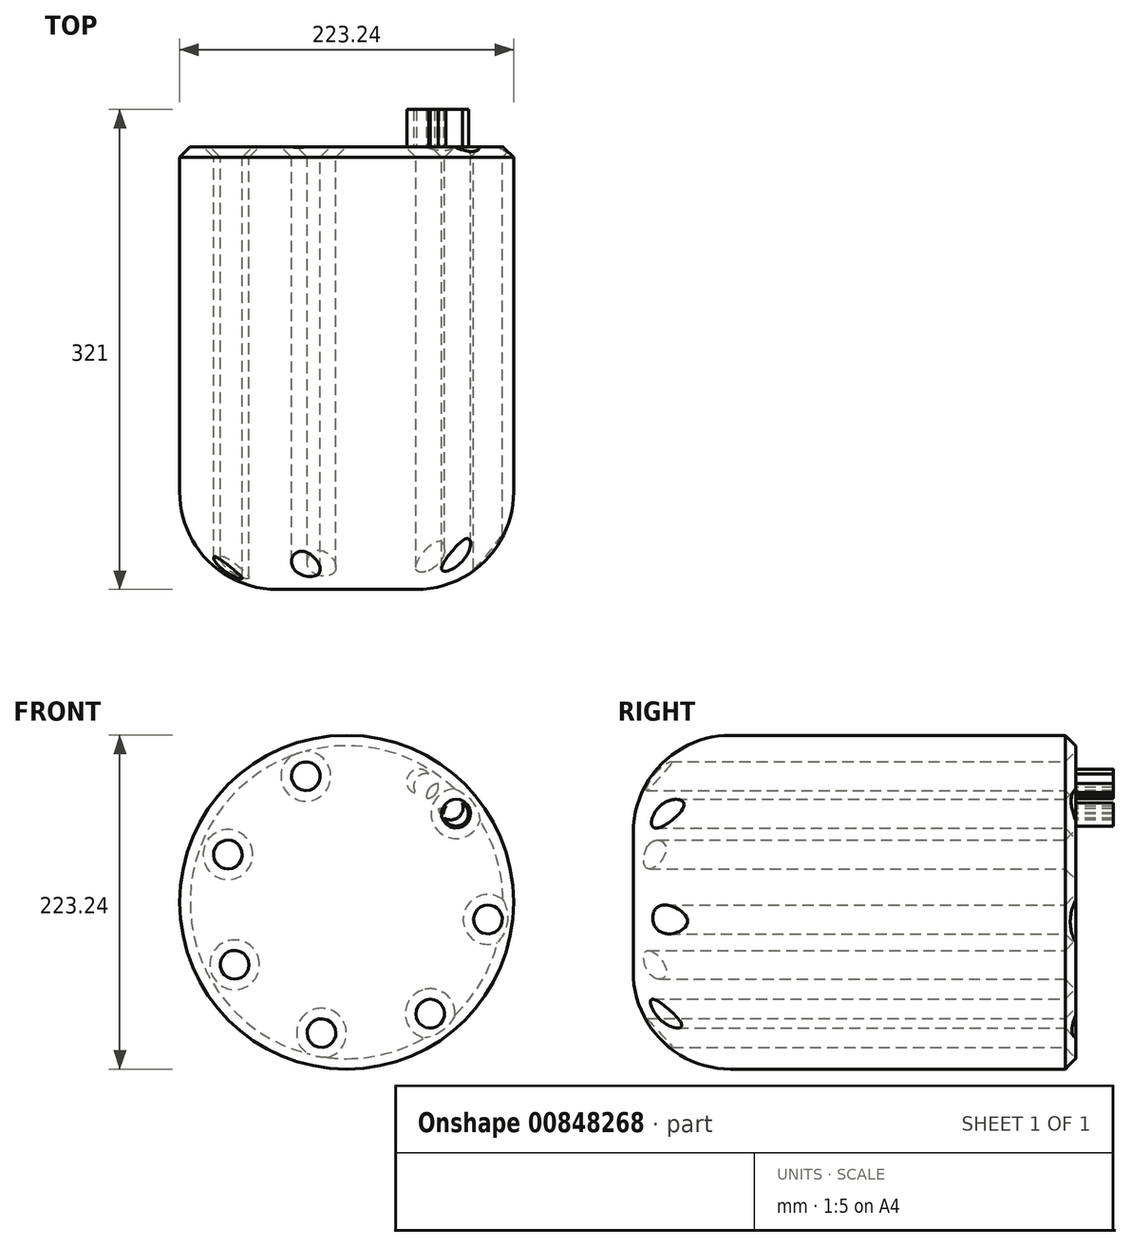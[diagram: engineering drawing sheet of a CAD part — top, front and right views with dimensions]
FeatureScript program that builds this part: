
annotation { "Feature Type Name" : "Feature", "Feature Type Description" : "" }
export const myFeature = defineFeature(function(context is Context, id is Id, definition is map)
    precondition{}
    {
        {
            var Q0;
            Q0=qCreatedBy(makeId("Front.planeOp"),FACE);
            var sketch = newSketch(context, id + "F0", { "sketchPlane" : qUnion([Q0])});
            skCircle(sketch, "E0", {"center": v(0, 0) * mm, "radius": 111.62 * mm});
            skCircle(sketch, "E1", {"center": v(73.16, 59.18) * mm, "radius": 9.64 * mm});
            skCircle(sketch, "E2.1.0", {"center": v(94.52, -11.55) * mm, "radius": 9.64 * mm});
            skCircle(sketch, "E2.2.0", {"center": v(55.9, -74.53) * mm, "radius": 9.64 * mm});
            skPoint(sketch, "E2.center", {"position": v(5.03, 0) * mm});
            skLineSegment(sketch, "E2.anchor1", {"start": v(5.03, 0) * mm, "end": v(73.16, 59.18) * mm, "construction": true});
            skLineSegment(sketch, "E2.anchor2", {"start": v(5.03, 0) * mm, "end": v(-27.28, 84.26) * mm, "construction": true});
            skCircle(sketch, "E3.1.3.0", {"center": v(-16.83, -87.55) * mm, "radius": 9.64 * mm});
            skCircle(sketch, "E3.1.4.0", {"center": v(-74.9, -41.87) * mm, "radius": 9.64 * mm});
            skCircle(sketch, "E4.1.5.0", {"center": v(-79.39, 31.88) * mm, "radius": 9.64 * mm});
            skCircle(sketch, "E4.1.6.0", {"center": v(-27.28, 84.26) * mm, "radius": 9.64 * mm});
            skSolve(sketch);
        }
        {
            var Q0;
            Q0=makeQuery(id+"F0.imprint","IMPRINT",FACE,{"disambiguationData":[TD([[makeQuery(id+"F0.imprint","IMPRINT",EDGE,{"derivedFrom":sQuery(id+"F0.wireOp",EDGE,"E0")}),1.0]])]});
            extrude(context, id + "F1", {"entities" : qUnion([Q0]), "depth" : 296 * mm, "offsetDistance" : 25 * mm});
        }
        {
            var Q0;
            Q0=makeQuery(id+"F1.opExtrude","CAP_EDGE",EDGE,{"disambiguationData":[OSD([sQuery(id+"F0.wireOp",EDGE,"E0")])],"isStart":false});
            fillet(context, id + "F2", {"entities" : qUnion([Q0]), "radius" : 65.18 * mm, "tangentPropagation" : true, "allowEdgeOverflow" : false});
        }
        {
            var Q0;
            Q0=makeQuery(id+"F1.opExtrude","CAP_EDGE",EDGE,{"disambiguationData":[OSD([sQuery(id+"F0.wireOp",EDGE,"E4.1.6.0")])],"isStart":true});
            var Q1;
            Q1=makeQuery(id+"F1.opExtrude","CAP_EDGE",EDGE,{"disambiguationData":[OSD([sQuery(id+"F0.wireOp",EDGE,"E4.1.5.0")])],"isStart":true});
            var Q2;
            Q2=makeQuery(id+"F1.opExtrude","CAP_FACE",FACE,{"disambiguationData":[OSD([sQuery(id+"F0.wireOp",EDGE,"E0"),sQuery(id+"F0.wireOp",EDGE,"E1"),sQuery(id+"F0.wireOp",EDGE,"E2.1.0"),sQuery(id+"F0.wireOp",EDGE,"E2.2.0"),sQuery(id+"F0.wireOp",EDGE,"E3.1.3.0"),sQuery(id+"F0.wireOp",EDGE,"E3.1.4.0"),sQuery(id+"F0.wireOp",EDGE,"E4.1.5.0"),sQuery(id+"F0.wireOp",EDGE,"E4.1.6.0")])],"isStart":true});
            chamfer(context, id + "F3", {"entities" : qUnion([Q0, Q1, Q2]), "width" : 7 * mm, "tangentPropagation" : true});
        }
        {
            var Q0;
            Q0=makeQuery(id+"F1.opExtrude","CAP_FACE",FACE,{"disambiguationData":[OSD([sQuery(id+"F0.wireOp",EDGE,"E0"),sQuery(id+"F0.wireOp",EDGE,"E1"),sQuery(id+"F0.wireOp",EDGE,"E2.1.0"),sQuery(id+"F0.wireOp",EDGE,"E2.2.0"),sQuery(id+"F0.wireOp",EDGE,"E3.1.3.0"),sQuery(id+"F0.wireOp",EDGE,"E3.1.4.0"),sQuery(id+"F0.wireOp",EDGE,"E4.1.5.0"),sQuery(id+"F0.wireOp",EDGE,"E4.1.6.0")])],"isStart":true});
            var sketch = newSketch(context, id + "F4", { "sketchPlane" : qUnion([Q0])});
            skCircle(sketch, "E5", {"center": v(-73.16, 59.18) * mm, "radius": 8.3 * mm});
            skCircle(sketch, "E6.1.0", {"center": v(-69.6, 63.33) * mm, "radius": 8.3 * mm});
            skCircle(sketch, "E6.2.0", {"center": v(-65.8, 67.27) * mm, "radius": 8.3 * mm});
            skCircle(sketch, "E6.3.0", {"center": v(-61.77, 70.98) * mm, "radius": 8.3 * mm});
            skCircle(sketch, "E6.4.0", {"center": v(-57.54, 74.45) * mm, "radius": 8.3 * mm});
            skCircle(sketch, "E6.5.0", {"center": v(-53.11, 77.67) * mm, "radius": 8.3 * mm});
            skCircle(sketch, "E6.6.0", {"center": v(-48.5, 80.63) * mm, "radius": 8.3 * mm});
            skPoint(sketch, "E6.center", {"position": v(0, 0) * mm});
            skLineSegment(sketch, "E6.anchor1", {"start": v(0, 0) * mm, "end": v(-73.16, 59.18) * mm, "construction": true});
            skLineSegment(sketch, "E6.anchor2", {"start": v(0, 0) * mm, "end": v(-48.5, 80.63) * mm, "construction": true});
            skSolve(sketch);
        }
        {
            var Q0;
            {var subQ0=sQuery(id+"F4.wireOp",EDGE,"E6.6.0");var subQ1=sQuery(id+"F4.wireOp",EDGE,"E6.5.0");var subQ2=makeQuery(id+"F4.imprint","INTERSECT",VERTEX,{"disambiguationData":[OD(0.0)],"derivedFrom":[subQ1,subQ0]});Q0=makeQuery(id+"F4.imprint","IMPRINT",FACE,{"disambiguationData":[TD([[makeQuery(id+"F4.imprint","IMPRINT",EDGE,{"disambiguationData":[TD([[subQ2,1.0]])],"derivedFrom":subQ1}),-1.0]])]});}
            var Q1;
            {var subQ3=sQuery(id+"F4.wireOp",EDGE,"E6.5.0");var subQ7=sQuery(id+"F4.wireOp",EDGE,"E6.2.0");var subQ9=makeQuery(id+"F4.imprint","INTERSECT",VERTEX,{"disambiguationData":[OD(0.0)],"derivedFrom":[subQ7,subQ3]});Q1=makeQuery(id+"F4.imprint","IMPRINT",FACE,{"disambiguationData":[TD([[makeQuery(id+"F4.imprint","IMPRINT",EDGE,{"disambiguationData":[TD([[subQ9,-1.0]])],"derivedFrom":subQ7}),-1.0]])]});}
            var Q2;
            {var subQ0=sQuery(id+"F4.wireOp",EDGE,"E6.3.0");var subQ1=sQuery(id+"F4.wireOp",EDGE,"E5");var subQ2=makeQuery(id+"F4.imprint","INTERSECT",VERTEX,{"disambiguationData":[OD(0.0)],"derivedFrom":[subQ1,subQ0]});Q2=makeQuery(id+"F4.imprint","IMPRINT",FACE,{"disambiguationData":[TD([[makeQuery(id+"F4.imprint","IMPRINT",EDGE,{"disambiguationData":[TD([[subQ2,1.0]])],"derivedFrom":subQ1}),-1.0]])]});}
            var Q3;
            {var subQ0=sQuery(id+"F4.wireOp",EDGE,"E6.1.0");var subQ1=sQuery(id+"F4.wireOp",EDGE,"E5");var subQ2=makeQuery(id+"F4.imprint","INTERSECT",VERTEX,{"disambiguationData":[OD(0.0)],"derivedFrom":[subQ1,subQ0]});Q3=makeQuery(id+"F4.imprint","IMPRINT",FACE,{"disambiguationData":[TD([[makeQuery(id+"F4.imprint","IMPRINT",EDGE,{"disambiguationData":[TD([[subQ2,-1.0]])],"derivedFrom":subQ1}),1.0]])]});}
            extrude(context, id + "F5", {"entities" : qUnion([Q0, Q1, Q2, Q3]), "operationType" : NewBodyOperationType.ADD, "depth" : 25 * mm, "offsetDistance" : 25 * mm});
        }
    });
